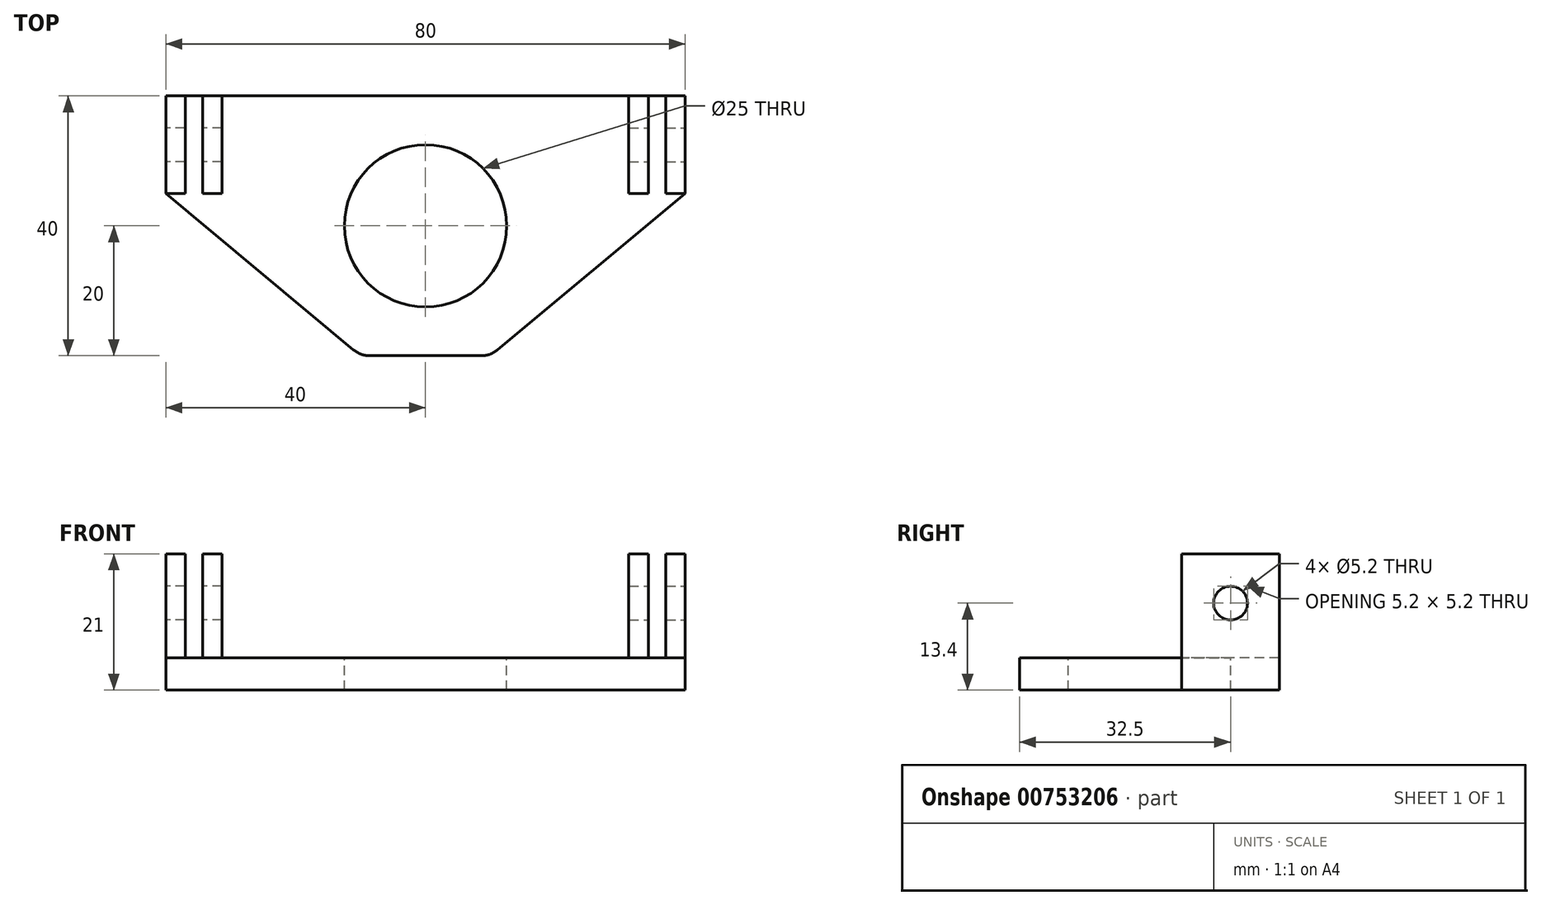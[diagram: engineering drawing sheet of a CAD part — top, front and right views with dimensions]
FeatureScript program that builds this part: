
annotation { "Feature Type Name" : "Feature", "Feature Type Description" : "" }
export const myFeature = defineFeature(function(context is Context, id is Id, definition is map)
    precondition{}
    {
        {
            var Q0;
            Q0=qCreatedBy(makeId("Top.planeOp"),FACE);
            var sketch = newSketch(context, id + "F0", { "sketchPlane" : qUnion([Q0])});
            skLineSegment(sketch, "E0", {"start": v(-40, 0) * mm, "end": v(0, 0) * mm});
            skLineSegment(sketch, "E1", {"start": v(-40, 0) * mm, "end": v(-40, -15) * mm});
            skLineSegment(sketch, "E2", {"start": v(-40, -15) * mm, "end": v(-10, -40) * mm});
            skLineSegment(sketch, "E3", {"start": v(-10, -40) * mm, "end": v(0, -40) * mm});
            skLineSegment(sketch, "E4", {"start": v(0, -40) * mm, "end": v(0, 0) * mm});
            skLineSegment(sketch, "E5.bottom", {"start": v(-40, 0) * mm, "end": v(-37, 0) * mm});
            skLineSegment(sketch, "E5.top", {"start": v(-40, -15) * mm, "end": v(-37, -15) * mm});
            skLineSegment(sketch, "E5.right", {"start": v(-37, 0) * mm, "end": v(-37, -15) * mm});
            skLineSegment(sketch, "E6.bottom", {"start": v(-34.3, 0) * mm, "end": v(-31.3, 0) * mm});
            skLineSegment(sketch, "E6.top", {"start": v(-34.3, -15) * mm, "end": v(-31.3, -15) * mm});
            skLineSegment(sketch, "E6.left", {"start": v(-34.3, 0) * mm, "end": v(-34.3, -15) * mm});
            skLineSegment(sketch, "E6.right", {"start": v(-31.3, 0) * mm, "end": v(-31.3, -15) * mm});
            skArc(sketch, "E7", {"start": v(0, -7.5) * mm, "mid": v(-12.5, -20) * mm, "end": v(0, -32.5) * mm});
            skSolve(sketch);
        }
        {
            var Q0;
            Q0=makeQuery(id+"F0.imprint","IMPRINT",FACE,{"disambiguationData":[TD([[makeQuery(id+"F0.imprint","IMPRINT",EDGE,{"derivedFrom":sQuery(id+"F0.wireOp",EDGE,"E2")}),1.0]])]});
            var Q1;
            Q1=makeQuery(id+"F0.imprint","IMPRINT",FACE,{"disambiguationData":[TD([[makeQuery(id+"F0.imprint","IMPRINT",EDGE,{"derivedFrom":sQuery(id+"F0.wireOp",EDGE,"E6.top")}),1.0]])]});
            var Q2;
            {var subQ0=sQuery(id+"F0.wireOp",EDGE,"E1");Q2=makeQuery(id+"F0.imprint","IMPRINT",FACE,{"disambiguationData":[TD([[makeQuery(id+"F0.imprint","IMPRINT",EDGE,{"derivedFrom":subQ0}),1.0]])]});}
            extrude(context, id + "F1", {"entities" : qUnion([Q0, Q1, Q2]), "oppositeDirection" : true, "depth" : 5 * mm, "offsetDistance" : 25 * mm});
        }
        {
            var Q0;
            Q0=makeQuery(id+"F0.imprint","IMPRINT",FACE,{"disambiguationData":[TD([[makeQuery(id+"F0.imprint","IMPRINT",EDGE,{"derivedFrom":sQuery(id+"F0.wireOp",EDGE,"E6.top")}),1.0]])]});
            var Q1;
            {var subQ0=sQuery(id+"F0.wireOp",EDGE,"E1");Q1=makeQuery(id+"F0.imprint","IMPRINT",FACE,{"disambiguationData":[TD([[makeQuery(id+"F0.imprint","IMPRINT",EDGE,{"derivedFrom":subQ0}),1.0]])]});}
            extrude(context, id + "F2", {"entities" : qUnion([Q0, Q1]), "operationType" : NewBodyOperationType.ADD, "depth" : 16 * mm, "offsetDistance" : 25 * mm});
        }
        {
            var Q0;
            Q0=makeQuery(id+"F2.opExtrude","CAP_EDGE",EDGE,{"disambiguationData":[OSD([sQuery(id+"F0.wireOp",EDGE,"E6.top")])],"isStart":true});
            var Q1;
            Q1=makeQuery(id+"F1.opExtrude","SWEPT_EDGE",EDGE,{"disambiguationData":[OSD([sQuery(id+"F0.wireOp",EDGE,"E2"),sQuery(id+"F0.wireOp",EDGE,"E3")])]});
            var Q2;
            Q2=makeQuery(id+"F2.opExtrude","CAP_EDGE",EDGE,{"disambiguationData":[OSD([sQuery(id+"F0.wireOp",EDGE,"E5.top")])],"isStart":true});
            fillet(context, id + "F3", {"entities" : qUnion([Q0, Q1, Q2]), "radius" : 4 * mm, "tangentPropagation" : true, "rho" : 0.5, "crossSection" : FilletCrossSection.CONIC, "allowEdgeOverflow" : false});
        }
        {
            var Q0;
            {var subQ0=sQuery(id+"F0.wireOp",EDGE,"E1");Q0=makeQuery(id+"F2.boolean.opBoolean","MERGE",FACE,{"derivedFrom":[makeQuery(id+"F1.opExtrude","SWEPT_FACE",FACE,{"disambiguationData":[OSD([subQ0])]}),makeQuery(id+"F2.opExtrude","SWEPT_FACE",FACE,{"disambiguationData":[OSD([subQ0])]})]});}
            var sketch = newSketch(context, id + "F4", { "sketchPlane" : qUnion([Q0])});
            skCircle(sketch, "E8", {"center": v(7.5, 8.4) * mm, "radius": 2.6 * mm});
            skPoint(sketch, "E8.centerSnap0", {"position": v(7.5, 16) * mm});
            skSolve(sketch);
        }
        {
            var Q0;
            Q0=makeQuery(id+"F4.imprint","IMPRINT",FACE,{"disambiguationData":[TD([[makeQuery(id+"F4.imprint","IMPRINT",EDGE,{"derivedFrom":sQuery(id+"F4.wireOp",EDGE,"E8")}),1.0]])]});
            extrude(context, id + "F5", {"entities" : qUnion([Q0]), "operationType" : NewBodyOperationType.REMOVE, "endBound" : BoundingType.THROUGH_ALL, "oppositeDirection" : true, "depth" : 25 * mm, "offsetDistance" : 25 * mm});
        }
        {
            var Q0;
            Q0=makeQuery(id+"F1.opExtrude","SWEPT_BODY",BODY,{"disambiguationData":[OSD([sQuery(id+"F0.wireOp",EDGE,"E0"),sQuery(id+"F0.wireOp",EDGE,"E1"),sQuery(id+"F0.wireOp",EDGE,"E2"),sQuery(id+"F0.wireOp",EDGE,"E3"),sQuery(id+"F0.wireOp",EDGE,"E4"),sQuery(id+"F0.wireOp",EDGE,"E7")])]});
            var Q1;
            Q1=qCreatedBy(makeId("Right.planeOp"),FACE);
            mirror(context, id + "F6", {"operationType" : NewBodyOperationType.ADD, "entities" : qUnion([Q0]), "mirrorPlane" : qUnion([Q1])});
        }
    });
